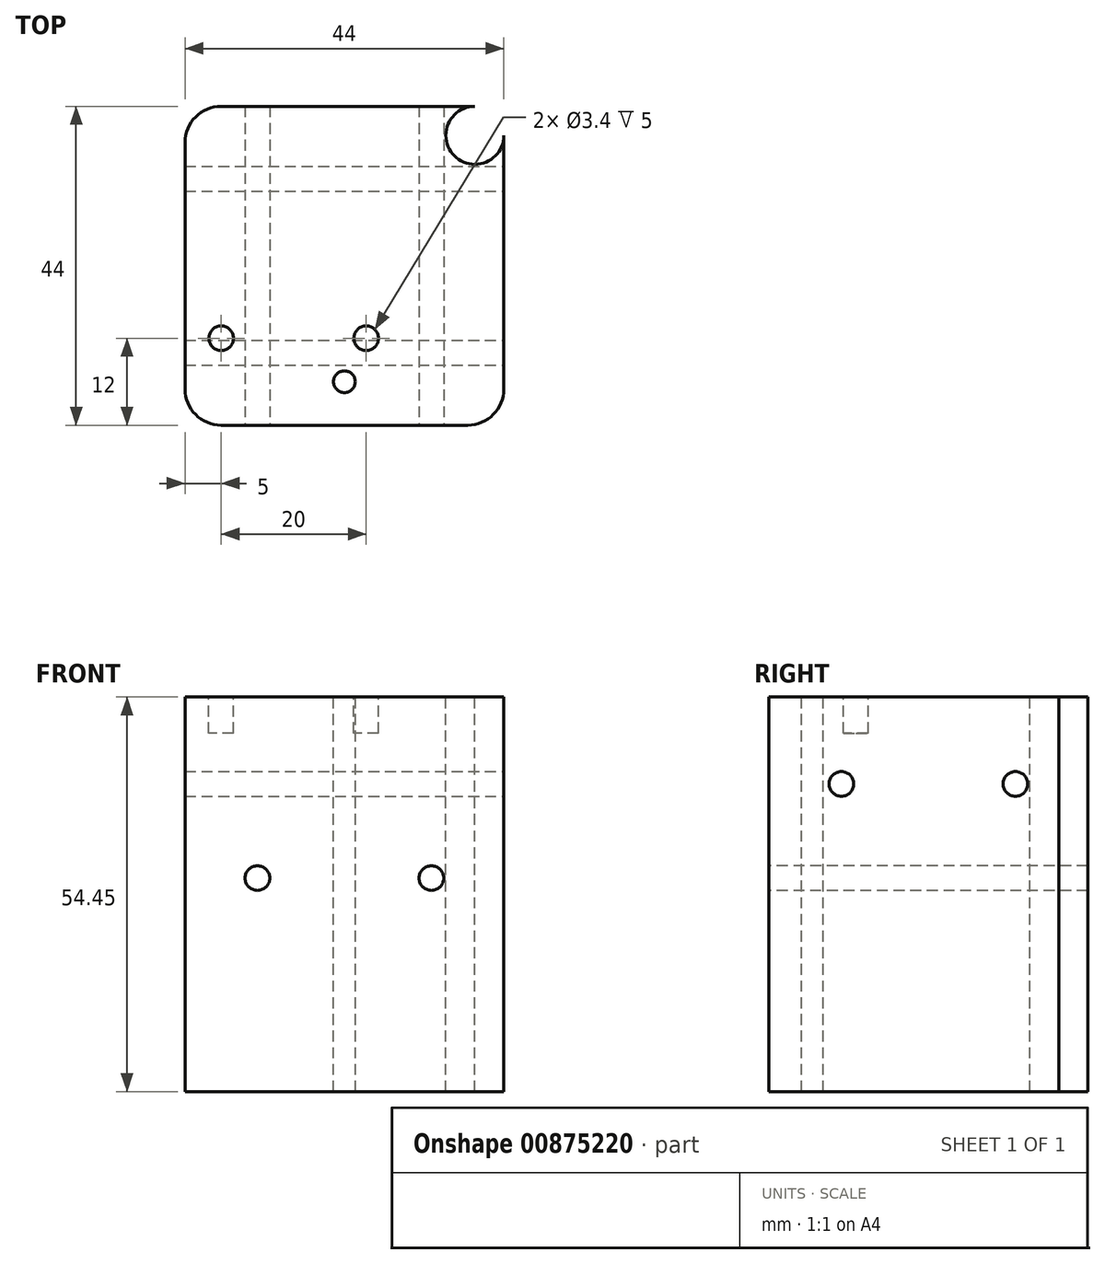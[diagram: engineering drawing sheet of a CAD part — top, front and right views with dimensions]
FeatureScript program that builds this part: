
annotation { "Feature Type Name" : "Feature", "Feature Type Description" : "" }
export const myFeature = defineFeature(function(context is Context, id is Id, definition is map)
    precondition{}
    {
        {
            var Q0;
            Q0=qCreatedBy(makeId("Top.planeOp"),FACE);
            var sketch = newSketch(context, id + "F0", { "sketchPlane" : qUnion([Q0])});
            skLineSegment(sketch, "E0.bottom", {"start": v(-22, 22) * mm, "end": v(22, 22) * mm});
            skLineSegment(sketch, "E0.top", {"start": v(-22, -22) * mm, "end": v(22, -22) * mm});
            skLineSegment(sketch, "E0.left", {"start": v(-22, 22) * mm, "end": v(-22, -22) * mm});
            skLineSegment(sketch, "E0.right", {"start": v(22, 22) * mm, "end": v(22, -22) * mm});
            skPoint(sketch, "E0.middle", {"position": v(0, 0) * mm});
            skCircle(sketch, "E1", {"center": v(18, 18) * mm, "radius": 4 * mm});
            skLineSegment(sketch, "E2", {"start": v(18, 18) * mm, "end": v(18, 22) * mm});
            skLineSegment(sketch, "E3", {"start": v(18, 18) * mm, "end": v(22, 18) * mm});
            skCircle(sketch, "E4", {"center": v(-17, -10) * mm, "radius": 1.7 * mm});
            skCircle(sketch, "E5", {"center": v(0, -16) * mm, "radius": 1.5 * mm});
            skCircle(sketch, "E6", {"center": v(3, -10) * mm, "radius": 1.7 * mm});
            skLineSegment(sketch, "E7", {"start": v(-22, -10) * mm, "end": v(22, -10) * mm, "construction": true});
            skSolve(sketch);
        }
        {
            var Q0;
            {var subQ1=sQuery(id+"F0.wireOp",EDGE,"E0.top");Q0=makeQuery(id+"F0.imprint","IMPRINT",FACE,{"disambiguationData":[TD([[makeQuery(id+"F0.imprint","IMPRINT",EDGE,{"derivedFrom":subQ1}),1.0]])]});}
            var Q1;
            Q1=makeQuery(id+"F0.imprint","IMPRINT",FACE,{"disambiguationData":[TD([[makeQuery(id+"F0.imprint","IMPRINT",EDGE,{"derivedFrom":sQuery(id+"F0.wireOp",EDGE,"E4")}),1.0]])]});
            var Q2;
            Q2=makeQuery(id+"F0.imprint","IMPRINT",FACE,{"disambiguationData":[TD([[makeQuery(id+"F0.imprint","IMPRINT",EDGE,{"derivedFrom":sQuery(id+"F0.wireOp",EDGE,"E5")}),1.0]])]});
            var Q3;
            Q3=makeQuery(id+"F0.imprint","IMPRINT",FACE,{"disambiguationData":[TD([[makeQuery(id+"F0.imprint","IMPRINT",EDGE,{"derivedFrom":sQuery(id+"F0.wireOp",EDGE,"E6")}),1.0]])]});
            extrude(context, id + "F1", {"entities" : qUnion([Q0, Q1, Q2, Q3]), "oppositeDirection" : true, "depth" : 54.45 * mm, "offsetDistance" : 25 * mm});
        }
        {
            var Q0;
            Q0=makeQuery(id+"F1.opExtrude","SWEPT_FACE",FACE,{"disambiguationData":[OSD([sQuery(id+"F0.wireOp",EDGE,"E0.top")])]});
            var sketch = newSketch(context, id + "F2", { "sketchPlane" : qUnion([Q0])});
            skCircle(sketch, "E8", {"center": v(-12, -25) * mm, "radius": 1.7 * mm});
            skCircle(sketch, "E9", {"center": v(12, -25) * mm, "radius": 1.7 * mm});
            skSolve(sketch);
        }
        {
            var Q0;
            Q0=makeQuery(id+"F2.imprint","IMPRINT",FACE,{"disambiguationData":[TD([[makeQuery(id+"F2.imprint","IMPRINT",EDGE,{"derivedFrom":sQuery(id+"F2.wireOp",EDGE,"E8")}),1.0]])]});
            var Q1;
            Q1=makeQuery(id+"F2.imprint","IMPRINT",FACE,{"disambiguationData":[TD([[makeQuery(id+"F2.imprint","IMPRINT",EDGE,{"derivedFrom":sQuery(id+"F2.wireOp",EDGE,"E9")}),1.0]])]});
            extrude(context, id + "F3", {"entities" : qUnion([Q0, Q1]), "operationType" : NewBodyOperationType.REMOVE, "oppositeDirection" : true, "depth" : 44 * mm, "offsetDistance" : 25 * mm});
        }
        {
            var Q0;
            Q0=makeQuery(id+"F1.opExtrude","SWEPT_FACE",FACE,{"disambiguationData":[OSD([sQuery(id+"F0.wireOp",EDGE,"E0.right")])]});
            var sketch = newSketch(context, id + "F4", { "sketchPlane" : qUnion([Q0])});
            skCircle(sketch, "E10", {"center": v(-12, -12) * mm, "radius": 1.7 * mm});
            skCircle(sketch, "E11", {"center": v(12, -12) * mm, "radius": 1.7 * mm});
            skSolve(sketch);
        }
        {
            var Q0;
            Q0=makeQuery(id+"F4.imprint","IMPRINT",FACE,{"disambiguationData":[TD([[makeQuery(id+"F4.imprint","IMPRINT",EDGE,{"derivedFrom":sQuery(id+"F4.wireOp",EDGE,"E10")}),1.0]])]});
            var Q1;
            Q1=makeQuery(id+"F4.imprint","IMPRINT",FACE,{"disambiguationData":[TD([[makeQuery(id+"F4.imprint","IMPRINT",EDGE,{"derivedFrom":sQuery(id+"F4.wireOp",EDGE,"E11")}),1.0]])]});
            extrude(context, id + "F5", {"entities" : qUnion([Q0, Q1]), "operationType" : NewBodyOperationType.REMOVE, "oppositeDirection" : true, "depth" : 44 * mm, "offsetDistance" : 25 * mm});
        }
        {
            var Q0;
            Q0=makeQuery(id+"F1.opExtrude","SWEPT_EDGE",EDGE,{"disambiguationData":[OSD([sQuery(id+"F0.wireOp",EDGE,"E0.top"),sQuery(id+"F0.wireOp",EDGE,"E0.right")])]});
            var Q1;
            Q1=makeQuery(id+"F1.opExtrude","SWEPT_EDGE",EDGE,{"disambiguationData":[OSD([sQuery(id+"F0.wireOp",EDGE,"E0.top"),sQuery(id+"F0.wireOp",EDGE,"E0.left")])]});
            var Q2;
            Q2=makeQuery(id+"F1.opExtrude","SWEPT_EDGE",EDGE,{"disambiguationData":[OSD([sQuery(id+"F0.wireOp",EDGE,"E0.bottom"),sQuery(id+"F0.wireOp",EDGE,"E0.left")])]});
            fillet(context, id + "F6", {"entities" : qUnion([Q0, Q1, Q2]), "radius" : 5 * mm, "tangentPropagation" : true, "allowEdgeOverflow" : false});
        }
        {
            var Q0;
            Q0=makeQuery(id+"F0.imprint","IMPRINT",FACE,{"disambiguationData":[TD([[makeQuery(id+"F0.imprint","IMPRINT",EDGE,{"derivedFrom":sQuery(id+"F0.wireOp",EDGE,"E5")}),1.0]])]});
            extrude(context, id + "F7", {"entities" : qUnion([Q0]), "operationType" : NewBodyOperationType.REMOVE, "oppositeDirection" : true, "depth" : 55 * mm, "offsetDistance" : 25 * mm});
        }
        {
            var Q0;
            Q0=makeQuery(id+"F0.imprint","IMPRINT",FACE,{"disambiguationData":[TD([[makeQuery(id+"F0.imprint","IMPRINT",EDGE,{"derivedFrom":sQuery(id+"F0.wireOp",EDGE,"E4")}),1.0]])]});
            var Q1;
            Q1=makeQuery(id+"F0.imprint","IMPRINT",FACE,{"disambiguationData":[TD([[makeQuery(id+"F0.imprint","IMPRINT",EDGE,{"derivedFrom":sQuery(id+"F0.wireOp",EDGE,"E6")}),1.0]])]});
            extrude(context, id + "F8", {"entities" : qUnion([Q0, Q1]), "operationType" : NewBodyOperationType.REMOVE, "oppositeDirection" : true, "depth" : 5 * mm, "offsetDistance" : 25 * mm});
        }
    });
